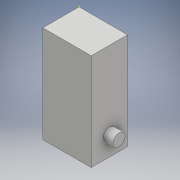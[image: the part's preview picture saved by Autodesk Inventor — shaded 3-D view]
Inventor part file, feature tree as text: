
AUTODESK INVENTOR PART (.ipt)
format: ipt  version: 2017 (Build 210142000, 142)  size: 104,448 bytes
history: native  units: mm
features: sketch x4, extrude x3
ambient origin geometry x8: Origin, YZ Plane, XZ Plane, XY Plane, X Axis, Y Axis, Z Axis, Center Point
bodies: Solid1 (feature_tree)
feature tree (7):
  extrude  "Extrusion1"  Depth=20.0mm
  sketch  "Sketch2"  dims[d2=2.5mm d3=10.0mm d4=0.0mm]
  sketch  "Sketch3"  dims[d5=2.0mm d6=0.0mm d7=10.0mm d8=0.0mm]
  extrude  "Extrusion2"  Depth=10.0mm TaperAngle=0.0deg
  extrude  "Extrusion3"  Depth=10.0mm TaperAngle=0.0deg
  sketch  "Sketch1"  dims[d0=7.5mm d1=20.0mm]
  sketch  "Sketch4"
